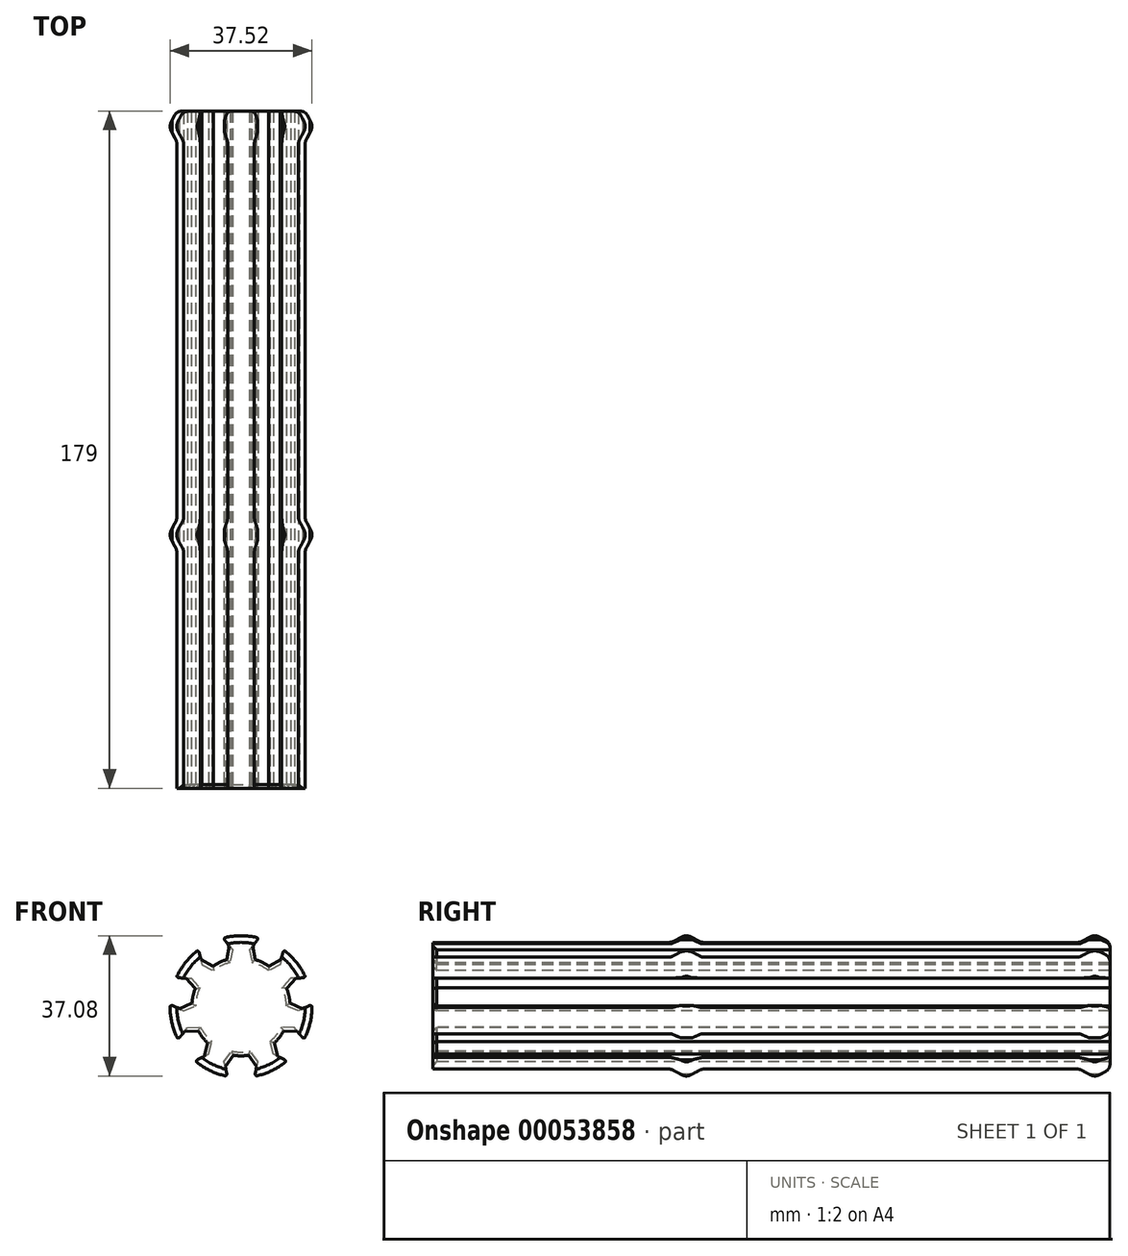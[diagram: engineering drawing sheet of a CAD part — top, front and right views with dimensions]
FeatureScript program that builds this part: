
annotation { "Feature Type Name" : "Feature", "Feature Type Description" : "" }
export const myFeature = defineFeature(function(context is Context, id is Id, definition is map)
    precondition{}
    {
        {
            var Q0;
            Q0=qCreatedBy(makeId("Top.planeOp"),FACE);
            var sketch = newSketch(context, id + "F0", { "sketchPlane" : qUnion([Q0])});
            skLineSegment(sketch, "E0", {"start": v(0, 0) * mm, "end": v(0, 180) * mm});
            skLineSegment(sketch, "E1", {"start": v(0, 0) * mm, "end": v(17, 0) * mm});
            skLineSegment(sketch, "E2", {"start": v(17, 0) * mm, "end": v(17, 64) * mm});
            skLineSegment(sketch, "E3", {"start": v(17, 64) * mm, "end": v(19, 68) * mm});
            skLineSegment(sketch, "E4", {"start": v(19, 68) * mm, "end": v(17, 72) * mm});
            skLineSegment(sketch, "E5", {"start": v(17, 72) * mm, "end": v(17, 172) * mm});
            skLineSegment(sketch, "E6", {"start": v(17, 172) * mm, "end": v(19, 176) * mm});
            skLineSegment(sketch, "E7", {"start": v(19, 176) * mm, "end": v(17, 180) * mm});
            skLineSegment(sketch, "E8", {"start": v(17, 180) * mm, "end": v(0, 180) * mm});
            skLineSegment(sketch, "E9", {"start": v(17, 180) * mm, "end": v(17, 172) * mm, "construction": true});
            skLineSegment(sketch, "E10", {"start": v(17, 72) * mm, "end": v(17, 64) * mm, "construction": true});
            skSolve(sketch);
        }
        {
            var Q0;
            Q0 = qSketchRegion(id + "F0", true);
            var Q1;
            Q1=sQuery(id+"F0.wireOp",EDGE,"E0");
            revolve(context, id + "F1", {"entities" : qUnion([Q0]), "axis" : qUnion([Q1]), "revolveType" : RevolveType.FULL});
        }
        {
            var Q0;
            Q0=makeQuery(id+"F1.opRevolve","SWEPT_EDGE",EDGE,{"disambiguationData":[OSD([sQuery(id+"F0.wireOp",EDGE,"E6"),sQuery(id+"F0.wireOp",EDGE,"E7")])]});
            var Q1;
            Q1=makeQuery(id+"F1.opRevolve","SWEPT_EDGE",EDGE,{"disambiguationData":[OSD([sQuery(id+"F0.wireOp",EDGE,"E5"),sQuery(id+"F0.wireOp",EDGE,"E6")])]});
            var Q2;
            Q2=makeQuery(id+"F1.opRevolve","SWEPT_EDGE",EDGE,{"disambiguationData":[OSD([sQuery(id+"F0.wireOp",EDGE,"E4"),sQuery(id+"F0.wireOp",EDGE,"E5")])]});
            var Q3;
            Q3=makeQuery(id+"F1.opRevolve","SWEPT_EDGE",EDGE,{"disambiguationData":[OSD([sQuery(id+"F0.wireOp",EDGE,"E3"),sQuery(id+"F0.wireOp",EDGE,"E4")])]});
            var Q4;
            Q4=makeQuery(id+"F1.opRevolve","SWEPT_EDGE",EDGE,{"disambiguationData":[OSD([sQuery(id+"F0.wireOp",EDGE,"E2"),sQuery(id+"F0.wireOp",EDGE,"E3")])]});
            var Q5;
            Q5=makeQuery(id+"F1.opRevolve","SWEPT_EDGE",EDGE,{"disambiguationData":[OSD([sQuery(id+"F0.wireOp",EDGE,"E7"),sQuery(id+"F0.wireOp",EDGE,"E8")])]});
            fillet(context, id + "F2", {"entities" : qUnion([Q0, Q1, Q2, Q3, Q4, Q5]), "radius" : 2 * mm, "tangentPropagation" : true, "allowEdgeOverflow" : false});
        }
        {
            var Q0;
            Q0=qCreatedBy(makeId("Front.planeOp"),FACE);
            cPlane(context, id + "F3", {"entities" : qUnion([Q0]), "cplaneType" : CPlaneType.OFFSET, "offset" : 1 * mm, "oppositeDirection" : true, "width" : 150 * mm, "height" : 150 * mm});
        }
        {
            var Q0;
            Q0=qCreatedBy(id+"F3.planeOp",FACE);
            var sketch = newSketch(context, id + "F4", { "sketchPlane" : qUnion([Q0])});
            skLineSegment(sketch, "E11", {"start": v(-2.45, -11.75) * mm, "end": v(-5, -24) * mm, "construction": true});
            skLineSegment(sketch, "E12", {"start": v(-5, -24) * mm, "end": v(0, -24) * mm});
            skLineSegment(sketch, "E13", {"start": v(0, -24) * mm, "end": v(5, -24) * mm});
            skLineSegment(sketch, "E14", {"start": v(5, -24) * mm, "end": v(2.45, -11.75) * mm, "construction": true});
            skLineSegment(sketch, "E15", {"start": v(0, -24) * mm, "end": v(0, 0) * mm, "construction": true});
            skArc(sketch, "E16", {"start": v(-2.45, -11.75) * mm, "mid": v(0, -12) * mm, "end": v(2.45, -11.75) * mm});
            skLineSegment(sketch, "E17", {"start": v(-2.45, -11.75) * mm, "end": v(-4.46, -14.52) * mm});
            skLineSegment(sketch, "E18", {"start": v(-4.46, -14.52) * mm, "end": v(-3.72, -17.87) * mm});
            skLineSegment(sketch, "E19", {"start": v(-3.72, -17.87) * mm, "end": v(-5.74, -20.65) * mm});
            skLineSegment(sketch, "E20", {"start": v(-5.74, -20.65) * mm, "end": v(-5, -24) * mm});
            skLineSegment(sketch, "E21", {"start": v(-5.74, -20.65) * mm, "end": v(-4.46, -14.52) * mm, "construction": true});
            skLineSegment(sketch, "E22.MirrorCS", {"start": v(2.45, -11.75) * mm, "end": v(4.46, -14.52) * mm});
            skLineSegment(sketch, "E23.MirrorCS", {"start": v(4.46, -14.52) * mm, "end": v(3.72, -17.87) * mm});
            skLineSegment(sketch, "E24.MirrorCS", {"start": v(5.74, -20.65) * mm, "end": v(5, -24) * mm});
            skLineSegment(sketch, "E25.MirrorCS", {"start": v(3.72, -17.87) * mm, "end": v(5.74, -20.65) * mm});
            skArc(sketch, "E26.1.0", {"start": v(7.66, -9.24) * mm, "mid": v(9.38, -7.48) * mm, "end": v(10.71, -5.41) * mm});
            skLineSegment(sketch, "E26.1.1", {"start": v(7.66, -9.24) * mm, "end": v(8.57, -12.55) * mm});
            skLineSegment(sketch, "E26.1.2", {"start": v(8.57, -12.55) * mm, "end": v(11.65, -14.06) * mm});
            skLineSegment(sketch, "E26.1.3", {"start": v(11.65, -14.06) * mm, "end": v(12.57, -17.36) * mm});
            skLineSegment(sketch, "E26.1.4", {"start": v(12.57, -17.36) * mm, "end": v(15.65, -18.87) * mm});
            skLineSegment(sketch, "E26.1.5", {"start": v(15.65, -18.87) * mm, "end": v(18.76, -14.96) * mm});
            skLineSegment(sketch, "E26.1.6", {"start": v(18.76, -14.96) * mm, "end": v(21.88, -11.05) * mm});
            skLineSegment(sketch, "E26.1.7", {"start": v(19.72, -8.39) * mm, "end": v(21.88, -11.05) * mm});
            skLineSegment(sketch, "E26.1.8", {"start": v(16.3, -8.23) * mm, "end": v(19.72, -8.39) * mm});
            skLineSegment(sketch, "E26.1.9", {"start": v(14.14, -5.57) * mm, "end": v(16.3, -8.23) * mm});
            skLineSegment(sketch, "E26.1.10", {"start": v(10.71, -5.41) * mm, "end": v(14.14, -5.57) * mm});
            skArc(sketch, "E26.2.0", {"start": v(12, 0.23) * mm, "mid": v(11.7, 2.67) * mm, "end": v(10.9, 5) * mm});
            skLineSegment(sketch, "E26.2.1", {"start": v(12, 0.23) * mm, "end": v(15.15, -1.12) * mm});
            skLineSegment(sketch, "E26.2.2", {"start": v(15.15, -1.12) * mm, "end": v(18.25, 0.35) * mm});
            skLineSegment(sketch, "E26.2.3", {"start": v(18.25, 0.35) * mm, "end": v(21.4, -1) * mm});
            skLineSegment(sketch, "E26.2.4", {"start": v(21.4, -1) * mm, "end": v(24.51, 0.47) * mm});
            skLineSegment(sketch, "E26.2.5", {"start": v(24.51, 0.47) * mm, "end": v(23.4, 5.34) * mm});
            skLineSegment(sketch, "E26.2.6", {"start": v(23.4, 5.34) * mm, "end": v(22.29, 10.22) * mm});
            skLineSegment(sketch, "E26.2.7", {"start": v(18.85, 10.2) * mm, "end": v(22.29, 10.22) * mm});
            skLineSegment(sketch, "E26.2.8", {"start": v(16.6, 7.6) * mm, "end": v(18.85, 10.2) * mm});
            skLineSegment(sketch, "E26.2.9", {"start": v(13.17, 7.58) * mm, "end": v(16.6, 7.6) * mm});
            skLineSegment(sketch, "E26.2.10", {"start": v(10.9, 5) * mm, "end": v(13.17, 7.58) * mm});
            skArc(sketch, "E26.3.0", {"start": v(7.3, 9.52) * mm, "mid": v(5.2, 10.81) * mm, "end": v(2.9, 11.65) * mm});
            skLineSegment(sketch, "E26.3.1", {"start": v(7.3, 9.52) * mm, "end": v(10.32, 11.15) * mm});
            skLineSegment(sketch, "E26.3.2", {"start": v(10.32, 11.15) * mm, "end": v(11.11, 14.49) * mm});
            skLineSegment(sketch, "E26.3.3", {"start": v(11.11, 14.49) * mm, "end": v(14.13, 16.11) * mm});
            skLineSegment(sketch, "E26.3.4", {"start": v(14.13, 16.11) * mm, "end": v(14.92, 19.45) * mm});
            skLineSegment(sketch, "E26.3.5", {"start": v(14.92, 19.45) * mm, "end": v(10.41, 21.62) * mm});
            skLineSegment(sketch, "E26.3.6", {"start": v(10.41, 21.62) * mm, "end": v(5.9, 23.8) * mm});
            skLineSegment(sketch, "E26.3.7", {"start": v(3.79, 21.1) * mm, "end": v(5.9, 23.8) * mm});
            skLineSegment(sketch, "E26.3.8", {"start": v(4.4, 17.72) * mm, "end": v(3.79, 21.1) * mm});
            skLineSegment(sketch, "E26.3.9", {"start": v(2.28, 15.02) * mm, "end": v(4.4, 17.72) * mm});
            skLineSegment(sketch, "E26.3.10", {"start": v(2.9, 11.65) * mm, "end": v(2.28, 15.02) * mm});
            skArc(sketch, "E26.4.0", {"start": v(-2.9, 11.65) * mm, "mid": v(-5.2, 10.81) * mm, "end": v(-7.3, 9.52) * mm});
            skLineSegment(sketch, "E26.4.1", {"start": v(-2.9, 11.65) * mm, "end": v(-2.28, 15.02) * mm});
            skLineSegment(sketch, "E26.4.2", {"start": v(-2.28, 15.02) * mm, "end": v(-4.4, 17.72) * mm});
            skLineSegment(sketch, "E26.4.3", {"start": v(-4.4, 17.72) * mm, "end": v(-3.79, 21.1) * mm});
            skLineSegment(sketch, "E26.4.4", {"start": v(-3.79, 21.1) * mm, "end": v(-5.9, 23.8) * mm});
            skLineSegment(sketch, "E26.4.5", {"start": v(-5.9, 23.8) * mm, "end": v(-10.41, 21.62) * mm});
            skLineSegment(sketch, "E26.4.6", {"start": v(-10.41, 21.62) * mm, "end": v(-14.92, 19.45) * mm});
            skLineSegment(sketch, "E26.4.7", {"start": v(-14.13, 16.11) * mm, "end": v(-14.92, 19.45) * mm});
            skLineSegment(sketch, "E26.4.8", {"start": v(-11.11, 14.49) * mm, "end": v(-14.13, 16.11) * mm});
            skLineSegment(sketch, "E26.4.9", {"start": v(-10.32, 11.15) * mm, "end": v(-11.11, 14.49) * mm});
            skLineSegment(sketch, "E26.4.10", {"start": v(-7.3, 9.52) * mm, "end": v(-10.32, 11.15) * mm});
            skArc(sketch, "E26.5.0", {"start": v(-10.9, 5) * mm, "mid": v(-11.7, 2.67) * mm, "end": v(-12, 0.23) * mm});
            skLineSegment(sketch, "E26.5.1", {"start": v(-10.9, 5) * mm, "end": v(-13.17, 7.58) * mm});
            skLineSegment(sketch, "E26.5.2", {"start": v(-13.17, 7.58) * mm, "end": v(-16.6, 7.6) * mm});
            skLineSegment(sketch, "E26.5.3", {"start": v(-16.6, 7.6) * mm, "end": v(-18.85, 10.2) * mm});
            skLineSegment(sketch, "E26.5.4", {"start": v(-18.85, 10.2) * mm, "end": v(-22.29, 10.22) * mm});
            skLineSegment(sketch, "E26.5.5", {"start": v(-22.29, 10.22) * mm, "end": v(-23.4, 5.34) * mm});
            skLineSegment(sketch, "E26.5.6", {"start": v(-23.4, 5.34) * mm, "end": v(-24.51, 0.47) * mm});
            skLineSegment(sketch, "E26.5.7", {"start": v(-21.4, -1) * mm, "end": v(-24.51, 0.47) * mm});
            skLineSegment(sketch, "E26.5.8", {"start": v(-18.25, 0.35) * mm, "end": v(-21.4, -1) * mm});
            skLineSegment(sketch, "E26.5.9", {"start": v(-15.15, -1.12) * mm, "end": v(-18.25, 0.35) * mm});
            skLineSegment(sketch, "E26.5.10", {"start": v(-12, 0.23) * mm, "end": v(-15.15, -1.12) * mm});
            skArc(sketch, "E26.6.0", {"start": v(-10.71, -5.41) * mm, "mid": v(-9.38, -7.48) * mm, "end": v(-7.66, -9.24) * mm});
            skLineSegment(sketch, "E26.6.1", {"start": v(-10.71, -5.41) * mm, "end": v(-14.14, -5.57) * mm});
            skLineSegment(sketch, "E26.6.2", {"start": v(-14.14, -5.57) * mm, "end": v(-16.3, -8.23) * mm});
            skLineSegment(sketch, "E26.6.3", {"start": v(-16.3, -8.23) * mm, "end": v(-19.72, -8.39) * mm});
            skLineSegment(sketch, "E26.6.4", {"start": v(-19.72, -8.39) * mm, "end": v(-21.88, -11.05) * mm});
            skLineSegment(sketch, "E26.6.5", {"start": v(-21.88, -11.05) * mm, "end": v(-18.76, -14.96) * mm});
            skLineSegment(sketch, "E26.6.6", {"start": v(-18.76, -14.96) * mm, "end": v(-15.65, -18.87) * mm});
            skLineSegment(sketch, "E26.6.7", {"start": v(-12.57, -17.36) * mm, "end": v(-15.65, -18.87) * mm});
            skLineSegment(sketch, "E26.6.8", {"start": v(-11.65, -14.06) * mm, "end": v(-12.57, -17.36) * mm});
            skLineSegment(sketch, "E26.6.9", {"start": v(-8.57, -12.55) * mm, "end": v(-11.65, -14.06) * mm});
            skLineSegment(sketch, "E26.6.10", {"start": v(-7.66, -9.24) * mm, "end": v(-8.57, -12.55) * mm});
            skSolve(sketch);
        }
        {
            var Q0;
            Q0 = qSketchRegion(id + "F4", true);
            extrude(context, id + "F5", {"entities" : qUnion([Q0]), "operationType" : NewBodyOperationType.REMOVE, "endBound" : BoundingType.THROUGH_ALL, "oppositeDirection" : true, "depth" : 25 * mm});
        }
        {
            var Q0;
            Q0=makeQuery(id+"F5.boolean.opBoolean","COPY",EDGE,{"derivedFrom":makeQuery(id+"F5.opExtrude","CAP_EDGE",EDGE,{"disambiguationData":[OSD([sQuery(id+"F4.wireOp",EDGE,"E26.4.0")])],"isStart":true})});
            var Q1;
            Q1=makeQuery(id+"F5.boolean.opBoolean","COPY",EDGE,{"derivedFrom":makeQuery(id+"F5.opExtrude","CAP_EDGE",EDGE,{"disambiguationData":[OSD([sQuery(id+"F4.wireOp",EDGE,"E26.4.10")])],"isStart":true})});
            var Q2;
            Q2=makeQuery(id+"F5.boolean.opBoolean","COPY",EDGE,{"derivedFrom":makeQuery(id+"F5.opExtrude","CAP_EDGE",EDGE,{"disambiguationData":[OSD([sQuery(id+"F4.wireOp",EDGE,"E26.4.1")])],"isStart":true})});
            var Q3;
            Q3=makeQuery(id+"F5.boolean.opBoolean","COPY",EDGE,{"derivedFrom":makeQuery(id+"F5.opExtrude","CAP_EDGE",EDGE,{"disambiguationData":[OSD([sQuery(id+"F4.wireOp",EDGE,"E26.5.0")])],"isStart":true})});
            var Q4;
            Q4=makeQuery(id+"F5.boolean.opBoolean","COPY",EDGE,{"derivedFrom":makeQuery(id+"F5.opExtrude","CAP_EDGE",EDGE,{"disambiguationData":[OSD([sQuery(id+"F4.wireOp",EDGE,"E26.5.10")])],"isStart":true})});
            var Q5;
            Q5=makeQuery(id+"F5.boolean.opBoolean","COPY",EDGE,{"derivedFrom":makeQuery(id+"F5.opExtrude","CAP_EDGE",EDGE,{"disambiguationData":[OSD([sQuery(id+"F4.wireOp",EDGE,"E26.5.1")])],"isStart":true})});
            var Q6;
            Q6=makeQuery(id+"F5.boolean.opBoolean","COPY",EDGE,{"derivedFrom":makeQuery(id+"F5.opExtrude","CAP_EDGE",EDGE,{"disambiguationData":[OSD([sQuery(id+"F4.wireOp",EDGE,"E26.6.1")])],"isStart":true})});
            var Q7;
            Q7=makeQuery(id+"F5.boolean.opBoolean","COPY",EDGE,{"derivedFrom":makeQuery(id+"F5.opExtrude","CAP_EDGE",EDGE,{"disambiguationData":[OSD([sQuery(id+"F4.wireOp",EDGE,"E26.6.0")])],"isStart":true})});
            var Q8;
            Q8=makeQuery(id+"F5.boolean.opBoolean","COPY",EDGE,{"derivedFrom":makeQuery(id+"F5.opExtrude","CAP_EDGE",EDGE,{"disambiguationData":[OSD([sQuery(id+"F4.wireOp",EDGE,"E26.6.10")])],"isStart":true})});
            var Q9;
            Q9=makeQuery(id+"F5.boolean.opBoolean","COPY",EDGE,{"derivedFrom":makeQuery(id+"F5.opExtrude","CAP_EDGE",EDGE,{"disambiguationData":[OSD([sQuery(id+"F4.wireOp",EDGE,"E26.3.10")])],"isStart":true})});
            var Q10;
            Q10=makeQuery(id+"F5.boolean.opBoolean","COPY",EDGE,{"derivedFrom":makeQuery(id+"F5.opExtrude","CAP_EDGE",EDGE,{"disambiguationData":[OSD([sQuery(id+"F4.wireOp",EDGE,"E26.3.0")])],"isStart":true})});
            var Q11;
            Q11=makeQuery(id+"F5.boolean.opBoolean","COPY",EDGE,{"derivedFrom":makeQuery(id+"F5.opExtrude","CAP_EDGE",EDGE,{"disambiguationData":[OSD([sQuery(id+"F4.wireOp",EDGE,"E26.3.1")])],"isStart":true})});
            var Q12;
            Q12=makeQuery(id+"F5.boolean.opBoolean","COPY",EDGE,{"derivedFrom":makeQuery(id+"F5.opExtrude","CAP_EDGE",EDGE,{"disambiguationData":[OSD([sQuery(id+"F4.wireOp",EDGE,"E26.2.10")])],"isStart":true})});
            var Q13;
            Q13=makeQuery(id+"F5.boolean.opBoolean","COPY",EDGE,{"derivedFrom":makeQuery(id+"F5.opExtrude","CAP_EDGE",EDGE,{"disambiguationData":[OSD([sQuery(id+"F4.wireOp",EDGE,"E26.2.0")])],"isStart":true})});
            var Q14;
            Q14=makeQuery(id+"F5.boolean.opBoolean","COPY",EDGE,{"derivedFrom":makeQuery(id+"F5.opExtrude","CAP_EDGE",EDGE,{"disambiguationData":[OSD([sQuery(id+"F4.wireOp",EDGE,"E26.2.1")])],"isStart":true})});
            var Q15;
            Q15=makeQuery(id+"F5.boolean.opBoolean","COPY",EDGE,{"derivedFrom":makeQuery(id+"F5.opExtrude","CAP_EDGE",EDGE,{"disambiguationData":[OSD([sQuery(id+"F4.wireOp",EDGE,"E26.1.10")])],"isStart":true})});
            var Q16;
            Q16=makeQuery(id+"F5.boolean.opBoolean","COPY",EDGE,{"derivedFrom":makeQuery(id+"F5.opExtrude","CAP_EDGE",EDGE,{"disambiguationData":[OSD([sQuery(id+"F4.wireOp",EDGE,"E26.1.0")])],"isStart":true})});
            var Q17;
            Q17=makeQuery(id+"F5.boolean.opBoolean","COPY",EDGE,{"derivedFrom":makeQuery(id+"F5.opExtrude","CAP_EDGE",EDGE,{"disambiguationData":[OSD([sQuery(id+"F4.wireOp",EDGE,"E26.1.1")])],"isStart":true})});
            var Q18;
            Q18=makeQuery(id+"F5.boolean.opBoolean","COPY",EDGE,{"derivedFrom":makeQuery(id+"F5.opExtrude","CAP_EDGE",EDGE,{"disambiguationData":[OSD([sQuery(id+"F4.wireOp",EDGE,"E17")])],"isStart":true})});
            var Q19;
            Q19=makeQuery(id+"F5.boolean.opBoolean","COPY",EDGE,{"derivedFrom":makeQuery(id+"F5.opExtrude","CAP_EDGE",EDGE,{"disambiguationData":[OSD([sQuery(id+"F4.wireOp",EDGE,"E16")])],"isStart":true})});
            var Q20;
            Q20=makeQuery(id+"F5.boolean.opBoolean","COPY",EDGE,{"derivedFrom":makeQuery(id+"F5.opExtrude","CAP_EDGE",EDGE,{"disambiguationData":[OSD([sQuery(id+"F4.wireOp",EDGE,"E22.MirrorCS")])],"isStart":true})});
            chamfer(context, id + "F6", {"entities" : qUnion([Q0, Q1, Q2, Q3, Q4, Q5, Q6, Q7, Q8, Q9, Q10, Q11, Q12, Q13, Q14, Q15, Q16, Q17, Q18, Q19, Q20]), "width" : 1 * mm, "tangentPropagation" : true});
        }
        {
            var Q0;
            Q0=qCreatedBy(id+"F3.planeOp",FACE);
            var sketch = newSketch(context, id + "F7", { "sketchPlane" : qUnion([Q0])});
            skLineSegment(sketch, "E27.bottom", {"start": v(-31.42, 38.96) * mm, "end": v(69.73, 38.96) * mm});
            skLineSegment(sketch, "E27.top", {"start": v(-31.42, -106.1) * mm, "end": v(69.73, -106.1) * mm});
            skLineSegment(sketch, "E27.left", {"start": v(-31.42, 38.96) * mm, "end": v(-31.42, -106.1) * mm});
            skLineSegment(sketch, "E27.right", {"start": v(69.73, 38.96) * mm, "end": v(69.73, -106.1) * mm});
            skSolve(sketch);
        }
        {
            var Q0;
            Q0 = qSketchRegion(id + "F7", true);
            extrude(context, id + "F8", {"entities" : qUnion([Q0]), "operationType" : NewBodyOperationType.REMOVE, "depth" : 25 * mm});
        }
    });
